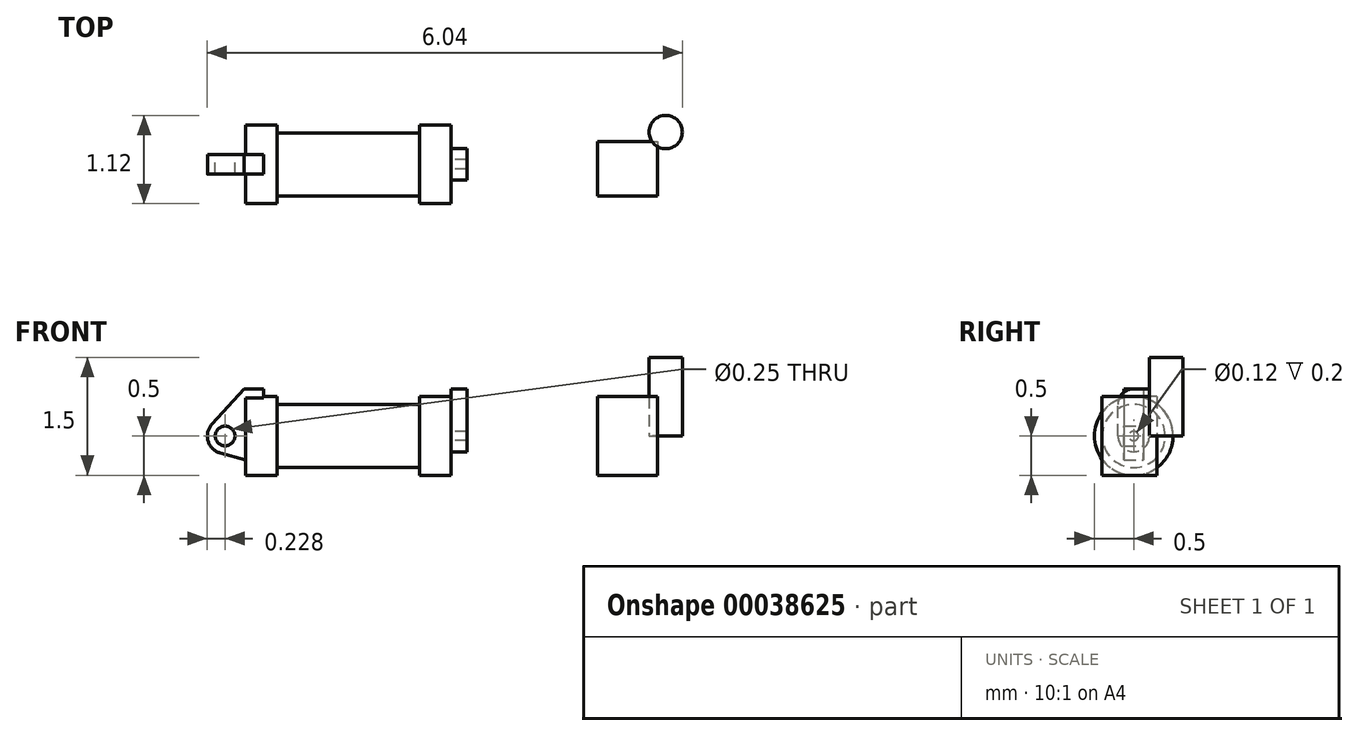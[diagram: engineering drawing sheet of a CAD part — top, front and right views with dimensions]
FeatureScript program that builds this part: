
annotation { "Feature Type Name" : "Feature", "Feature Type Description" : "" }
export const myFeature = defineFeature(function(context is Context, id is Id, definition is map)
    precondition{}
    {
        {
            var Q0;
            Q0=qCreatedBy(makeId("Front.planeOp"),FACE);
            var sketch = newSketch(context, id + "F0", { "sketchPlane" : qUnion([Q0])});
            skLineSegment(sketch, "E0.top", {"start": v(0, 0.5) * mm, "end": v(0.4, 0.5) * mm});
            skLineSegment(sketch, "E0.right", {"start": v(0.4, 0.4) * mm, "end": v(0.4, 0.5) * mm});
            skLineSegment(sketch, "E1.top", {"start": v(-0.02, 0.6) * mm, "end": v(0.23, 0.6) * mm});
            skCircle(sketch, "E2", {"center": v(-0.26, 0) * mm, "radius": 0.12 * mm});
            skCircle(sketch, "E3", {"center": v(-0.26, 0) * mm, "radius": 0.23 * mm});
            skLineSegment(sketch, "E4", {"start": v(0.23, 0.6) * mm, "end": v(0.23, -0.37) * mm});
            skLineSegment(sketch, "E5", {"start": v(0.23, -0.37) * mm, "end": v(-0.32, -0.22) * mm});
            skLineSegment(sketch, "E6", {"start": v(-0.02, 0.6) * mm, "end": v(-0.43, 0.15) * mm});
            skLineSegment(sketch, "E7.bottom", {"start": v(0, 0) * mm, "end": v(2.6, 0) * mm});
            skLineSegment(sketch, "E7.right", {"start": v(2.61, 0) * mm, "end": v(2.61, 0.5) * mm});
            skLineSegment(sketch, "E8", {"start": v(2.2, 0.5) * mm, "end": v(2.2, 0.4) * mm});
            skLineSegment(sketch, "E9", {"start": v(2.2, 0.4) * mm, "end": v(0.4, 0.4) * mm});
            skLineSegment(sketch, "E10.trimOffspring", {"start": v(2.2, 0.5) * mm, "end": v(2.6, 0.5) * mm});
            skLineSegment(sketch, "E11", {"start": v(0, 0.5) * mm, "end": v(0, 0) * mm});
            skSolve(sketch);
        }
        {
            var Q0;
            {var subQ3=sQuery(id+"F0.wireOp",EDGE,"E11");Q0=makeQuery(id+"F0.imprint","IMPRINT",FACE,{"disambiguationData":[TD([[makeQuery(id+"F0.imprint","IMPRINT",EDGE,{"derivedFrom":subQ3}),1.0]])]});}
            var Q1;
            {var subQ1=sQuery(id+"F0.wireOp",EDGE,"E0.right");Q1=makeQuery(id+"F0.imprint","IMPRINT",FACE,{"disambiguationData":[TD([[makeQuery(id+"F0.imprint","IMPRINT",EDGE,{"derivedFrom":subQ1}),1.0]])]});}
            var Q2;
            Q2=sQuery(id+"F0.wireOp",EDGE,"E7.bottom");
            revolve(context, id + "F1", {"entities" : qUnion([Q0, Q1]), "axis" : qUnion([Q2]), "revolveType" : RevolveType.FULL});
        }
        {
            var Q0;
            {var subQ3=sQuery(id+"F0.wireOp",EDGE,"E11");Q0=makeQuery(id+"F0.imprint","IMPRINT",FACE,{"disambiguationData":[TD([[makeQuery(id+"F0.imprint","IMPRINT",EDGE,{"derivedFrom":subQ3}),1.0]])]});}
            var Q1;
            {var subQ8=sQuery(id+"F0.wireOp",EDGE,"E1.top");Q1=makeQuery(id+"F0.imprint","IMPRINT",FACE,{"disambiguationData":[TD([[makeQuery(id+"F0.imprint","IMPRINT",EDGE,{"derivedFrom":subQ8}),-1.0]])]});}
            var Q2;
            Q2=makeQuery(id+"F0.imprint","IMPRINT",FACE,{"disambiguationData":[TD([[makeQuery(id+"F0.imprint","IMPRINT",EDGE,{"derivedFrom":sQuery(id+"F0.wireOp",EDGE,"E2")}),-1.0]])]});
            extrude(context, id + "F2", {"entities" : qUnion([Q0, Q1, Q2]), "operationType" : NewBodyOperationType.ADD, "endBound" : BoundingType.SYMMETRIC, "depth" : 0.25 * mm});
        }
        {
            var Q0;
            Q0=makeQuery(id+"F1.opRevolve","SWEPT_FACE",FACE,{"disambiguationData":[OSD([sQuery(id+"F0.wireOp",EDGE,"E7.right")])]});
            var sketch = newSketch(context, id + "F3", { "sketchPlane" : qUnion([Q0])});
            skCircle(sketch, "E12", {"center": v(0, 0) * mm, "radius": 0.06 * mm});
            skCircle(sketch, "E13", {"center": v(0, 0) * mm, "radius": 0.2 * mm});
            skLineSegment(sketch, "E14", {"start": v(-0.2, 0) * mm, "end": v(-0.2, 0.6) * mm});
            skLineSegment(sketch, "E15", {"start": v(0.2, 0) * mm, "end": v(0.2, 0.6) * mm});
            skLineSegment(sketch, "E16", {"start": v(0.2, 0.6) * mm, "end": v(-0.2, 0.6) * mm});
            skSolve(sketch);
        }
        {
            var Q0;
            {var subQ3=sQuery(id+"F3.wireOp",EDGE,"E14");var subQ5=sQuery(id+"F3.wireOp",EDGE,"E13");var subQ6=makeQuery(id+"F3.imprint","INTERSECT",VERTEX,{"derivedFrom":[subQ5,subQ3]});Q0=makeQuery(id+"F3.imprint","IMPRINT",FACE,{"disambiguationData":[TD([[makeQuery(id+"F3.imprint","IMPRINT",EDGE,{"disambiguationData":[TD([[subQ6,1.0]])],"derivedFrom":subQ5}),-1.0]])]});}
            var Q1;
            {var subQ5=sQuery(id+"F3.wireOp",EDGE,"E16");Q1=makeQuery(id+"F3.imprint","IMPRINT",FACE,{"disambiguationData":[TD([[makeQuery(id+"F3.imprint","IMPRINT",EDGE,{"derivedFrom":subQ5}),1.0]])]});}
            var Q2;
            Q2=makeQuery(id+"F3.imprint","IMPRINT",FACE,{"disambiguationData":[TD([[makeQuery(id+"F3.imprint","IMPRINT",EDGE,{"derivedFrom":sQuery(id+"F3.wireOp",EDGE,"E12")}),-1.0]])]});
            extrude(context, id + "F4", {"entities" : qUnion([Q0, Q1, Q2]), "operationType" : NewBodyOperationType.ADD, "depth" : 0.2 * mm});
        }
        {
            var Q0;
            Q0=makeQuery(id+"F4.opExtrude","SWEPT_EDGE",EDGE,{"disambiguationData":[OSD([sQuery(id+"F3.wireOp",EDGE,"E14"),sQuery(id+"F3.wireOp",EDGE,"E16")])]});
            fillet(context, id + "F5", {"entities" : qUnion([Q0]), "radius" : 0.2 * mm, "tangentPropagation" : true, "allowEdgeOverflow" : false});
        }
        {
            var Q0;
            Q0=qCreatedBy(makeId("Top.planeOp"),FACE);
            var sketch = newSketch(context, id + "F6", { "sketchPlane" : qUnion([Q0])});
            skLineSegment(sketch, "E17.bottom", {"start": v(4.47, 0.3) * mm, "end": v(5.23, 0.3) * mm});
            skLineSegment(sketch, "E17.top", {"start": v(4.47, -0.4) * mm, "end": v(5.23, -0.4) * mm});
            skLineSegment(sketch, "E17.left", {"start": v(4.47, 0.3) * mm, "end": v(4.47, -0.4) * mm});
            skLineSegment(sketch, "E17.right", {"start": v(5.23, 0.3) * mm, "end": v(5.23, -0.4) * mm});
            skSolve(sketch);
        }
        {
            var Q0;
            Q0 = qSketchRegion(id + "F6", true);
            extrude(context, id + "F7", {"entities" : qUnion([Q0]), "endBound" : BoundingType.SYMMETRIC, "depth" : 1 * mm});
        }
        {
            var Q0;
            Q0=qCreatedBy(makeId("Top.planeOp"),FACE);
            var sketch = newSketch(context, id + "F8", { "sketchPlane" : qUnion([Q0])});
            skCircle(sketch, "E18", {"center": v(5.64, 0.24) * mm, "radius": 0.21 * mm});
            skSolve(sketch);
        }
        {
            var Q0;
            Q0 = qSketchRegion(id + "F8", true);
            extrude(context, id + "F9", {"entities" : qUnion([Q0]), "depth" : 1 * mm});
        }
        {
            var Q0;
            Q0=makeQuery(id+"F9.opExtrude","SWEPT_BODY",BODY,{"disambiguationData":[OSD([sQuery(id+"F8.wireOp",EDGE,"E18")])]});
            transform(context, id + "F10", {"entities" : qUnion([Q0]), "transformType" : TransformType.TRANSLATION_3D, "dx" : -0.3 * mm, "dy" : 0.17 * mm, "dz" : 0 * mm, "makeCopy" : false});
        }
    });
